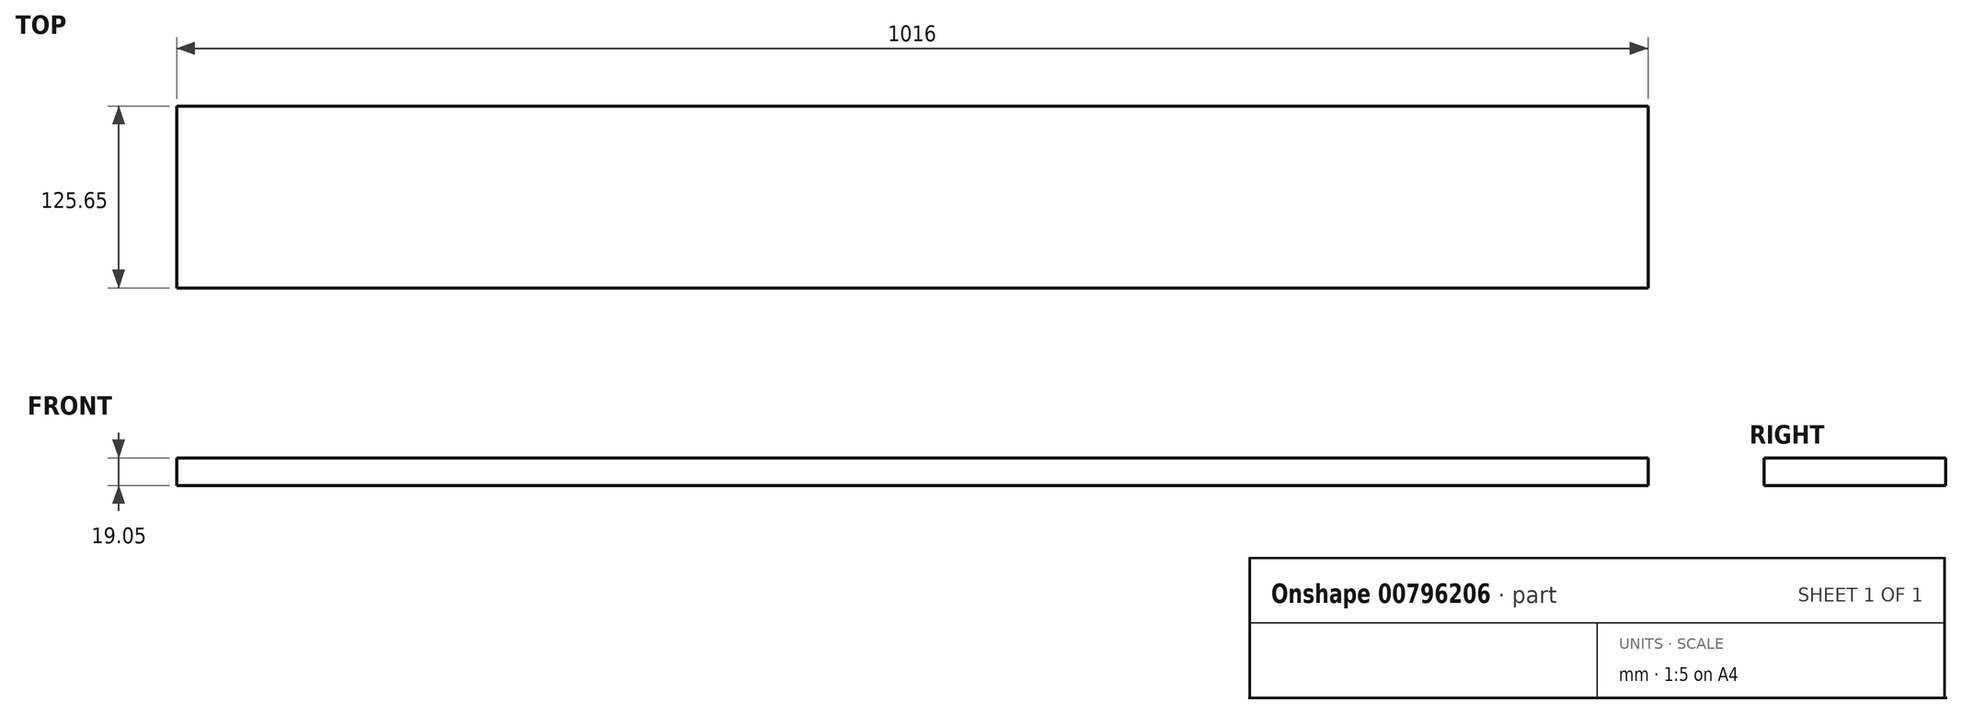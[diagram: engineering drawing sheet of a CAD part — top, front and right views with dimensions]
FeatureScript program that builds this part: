
annotation { "Feature Type Name" : "Feature", "Feature Type Description" : "" }
export const myFeature = defineFeature(function(context is Context, id is Id, definition is map)
    precondition{}
    {
        {
            var Q0;
            Q0=qCreatedBy(makeId("Top.planeOp"),FACE);
            var sketch = newSketch(context, id + "F0", { "sketchPlane" : qUnion([Q0])});
            skLineSegment(sketch, "E0.bottom", {"start": v(0, 0) * mm, "end": v(1016, 0) * mm});
            skLineSegment(sketch, "E0.top", {"start": v(0, -125.65) * mm, "end": v(1016, -125.65) * mm});
            skLineSegment(sketch, "E0.left", {"start": v(0, 0) * mm, "end": v(0, -125.65) * mm});
            skLineSegment(sketch, "E0.right", {"start": v(1016, 0) * mm, "end": v(1016, -125.65) * mm});
            skSolve(sketch);
        }
        {
            var Q0;
            Q0=makeQuery(id+"F0.imprint","IMPRINT",FACE,{"disambiguationData":[TD([[makeQuery(id+"F0.imprint","IMPRINT",EDGE,{"derivedFrom":sQuery(id+"F0.wireOp",EDGE,"E0.bottom")}),-1.0]])]});
            extrude(context, id + "F1", {"entities" : qUnion([Q0]), "depth" : 19.05 * mm, "offsetDistance" : 25.4 * mm});
        }
    });
